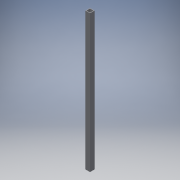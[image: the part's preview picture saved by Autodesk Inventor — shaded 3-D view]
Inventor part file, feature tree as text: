
AUTODESK INVENTOR PART (.ipt)
format: ipt  version: 2016 (Build 200138000, 138)  size: 110,080 bytes
history: native  units: in
note: dims shown in document units (in); Inventor stores cm internally (conversion verified against a paired STEP export)
features: extrude x2, sketch x2
ambient origin geometry x8: Origin, YZ Plane, XZ Plane, XY Plane, X Axis, Y Axis, Z Axis, Center Point
bodies: Solid1 (feature_tree)
feature tree (4):
  extrude  "Extrusion1"  Depth=1.0in
  extrude  "Extrusion2"  Depth=30.0in TaperAngle=0.0deg
  sketch  "Sketch1"  dims[d0=1.0in d1=1.0in]
  sketch  "Sketch2"  dims[d2=0.125in d3=30.0in d4=0.0in d5=0.5in d6=0.5in d7=0.5in d8=0.5in d9=0.5in d10=0.5in d11=1.0in d12=0.0in]
